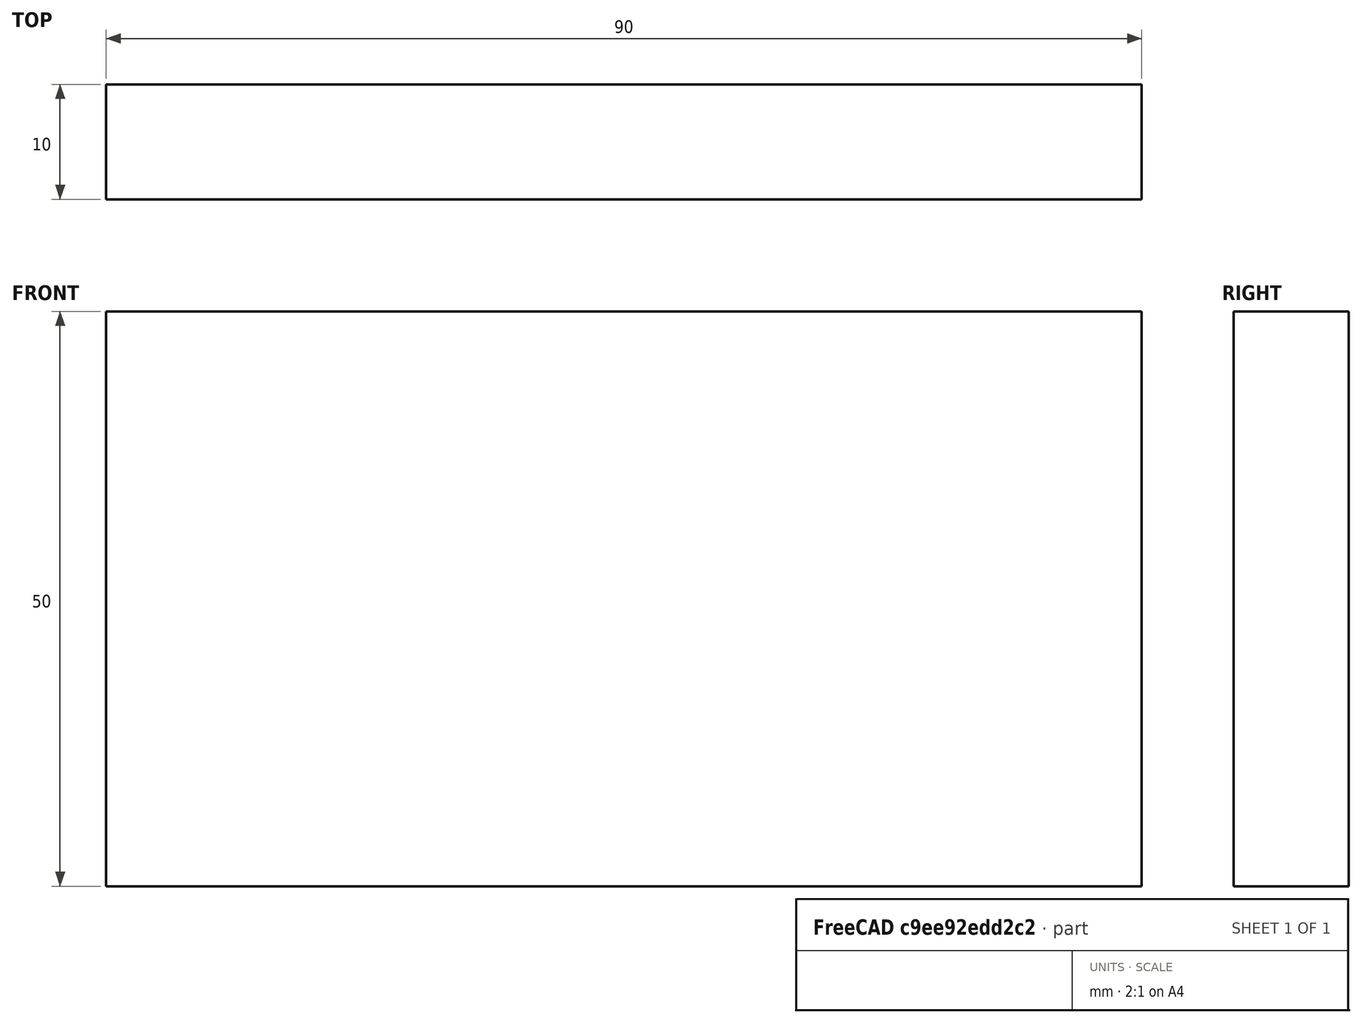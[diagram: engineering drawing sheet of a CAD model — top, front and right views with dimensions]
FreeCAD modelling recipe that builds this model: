
FCSTD DOCUMENT  (FreeCAD 0.15R4671 (Git))
Label: Flat Bar 90x10 EN10058 S235JR
License: All rights reserved
LicenseURL: http://en.wikipedia.org/wiki/All_rights_reserved
objects: Sketcher::SketchObject×1, Part::Extrusion×1
note: 2 computed .brp shape members not serialized (recipe doc carries the construction recipe); baked Part::Feature solids carry a one-line shape summary decoded from their .brp

FEATURE [Sketcher::SketchObject] Sketch
  sketch-geometry (4):
    g0: LineSegment StartX=-45 StartY=-5 StartZ=0 EndX=45 EndY=-5 EndZ=0
    g1: LineSegment StartX=45 StartY=-5 StartZ=0 EndX=45 EndY=5 EndZ=0
    g2: LineSegment StartX=45 StartY=5 StartZ=0 EndX=-45 EndY=5 EndZ=0
    g3: LineSegment StartX=-45 StartY=5 StartZ=0 EndX=-45 EndY=-5 EndZ=0
  constraints (12):
    c: Coincident(g0,g1)
    c: Coincident(g1,g2)
    c: Coincident(g2,g3)
    c: Coincident(g3,g0)
    c: Horizontal(g0)
    c: Horizontal(g2)
    c: Vertical(g1)
    c: Vertical(g3)
    c: Symmetric(g1,g2,g-2)
    c: Symmetric(g0,g1,g-1)
    c: DistanceY(g1) = 10
    c: DistanceX(g0) = 90
FEATURE [Part::Extrusion] Extrude  label="Flat Bar 90x10 EN10058 S235JR"
  Base = -> Sketch
  Dir = (0,0,50)
  Solid = true
